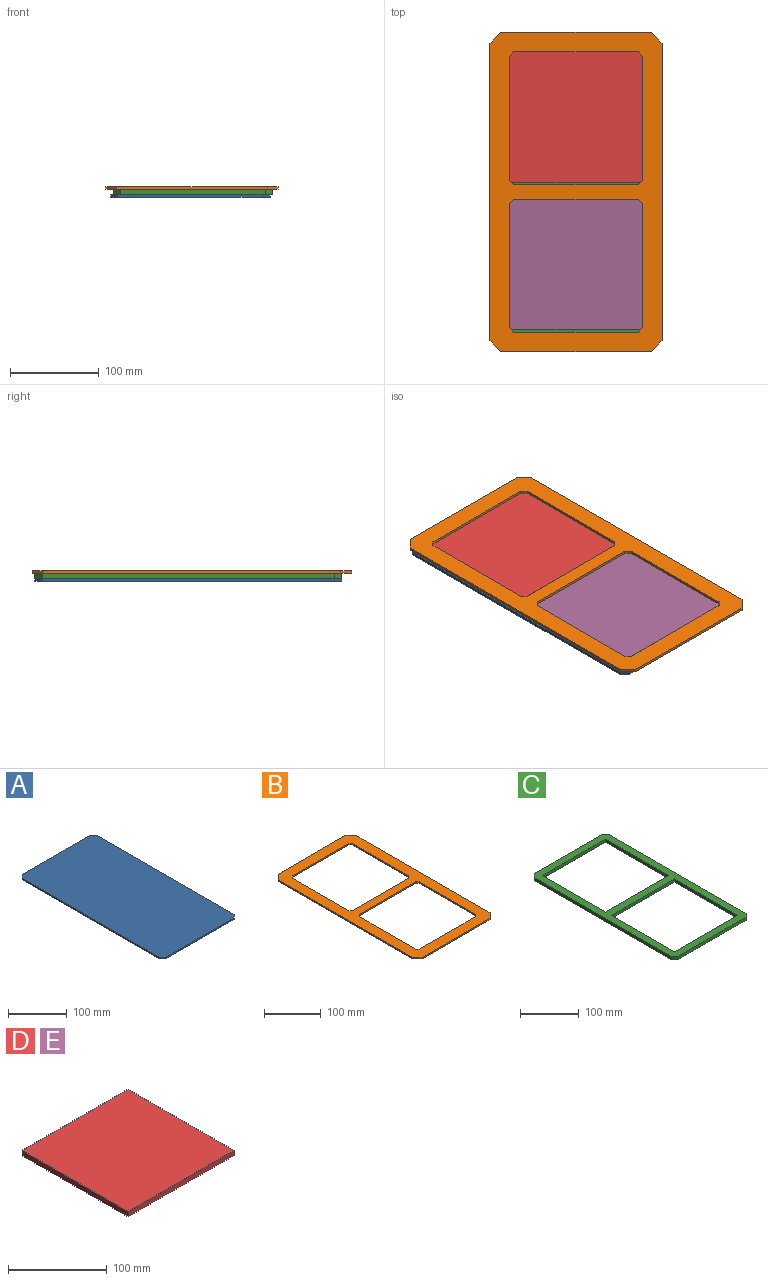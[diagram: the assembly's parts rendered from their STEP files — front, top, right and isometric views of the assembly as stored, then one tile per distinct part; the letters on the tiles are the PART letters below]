
ASSEMBLY  parts=5 mates=4
PART A: 10 faces, bbox 180x346x3 mm
  f0: plane 8.2x8.2mm, normal (-0.71,0.71,0), area 34.8mm2, adj f1,f7,f8,f9
  f1: plane 163.6x3mm, normal (0,1,0), area 490.8mm2, adj f0,f2,f8,f9
  f2: plane 8.2x8.2mm, normal (0.71,0.71,0), area 34.8mm2, adj f1,f3,f8,f9
  f3: plane 329.6x3mm, normal (1,0,0), area 988.8mm2, adj f2,f4,f8,f9
  f4: plane 8.2x8.2mm, normal (0.71,-0.71,0), area 34.8mm2, adj f3,f5,f8,f9
  f5: plane 163.6x3mm, normal (0,-1,0), area 490.8mm2, adj f4,f6,f8,f9
  f6: plane 8.2x8.2mm, normal (-0.71,-0.71,0), area 34.8mm2, adj f5,f7,f8,f9
  f7: plane 329.6x3mm, normal (-1,0,0), area 988.8mm2, adj f0,f6,f8,f9
  f8: plane 346x180mm, normal (0,0,-1), area 62145.5mm2, adj f0,f1,f2,f3,f4,f5,f6,f7
  f9: plane 346x180mm, normal (0,0,1), area 62145.5mm2, adj f0,f1,f2,f3,f4,f5,f6,f7
PART B: 26 faces, bbox 194x360x3 mm
  f0: plane 4.95x4.95mm, normal (0.71,0.71,0), area 21mm2, adj f1,f23,f24,f25
  f1: plane 140.1x3mm, normal (1,0,0), area 420.3mm2, adj f0,f2,f24,f25
  f2: plane 4.95x4.95mm, normal (0.71,-0.71,0), area 21mm2, adj f1,f3,f24,f25
  f3: plane 140.1x3mm, normal (0,-1,0), area 420.3mm2, adj f2,f4,f24,f25
  f4: plane 4.95x4.95mm, normal (-0.71,-0.71,0), area 21mm2, adj f3,f5,f24,f25
  f5: plane 140.1x3mm, normal (-1,0,0), area 420.3mm2, adj f4,f6,f24,f25
  f6: plane 4.95x4.95mm, normal (-0.71,0.71,0), area 21mm2, adj f5,f23,f24,f25
  f7: plane 140.1x3mm, normal (1,0,0), area 420.3mm2, adj f8,f21,f24,f25
  f8: plane 4.95x4.95mm, normal (0.71,-0.71,0), area 21mm2, adj f7,f9,f24,f25
  f9: plane 140.1x3mm, normal (0,-1,0), area 420.3mm2, adj f8,f10,f24,f25
  f10: plane 4.95x4.95mm, normal (-0.71,-0.71,0), area 21mm2, adj f9,f11,f24,f25
  f11: plane 140.1x3mm, normal (-1,0,0), area 420.3mm2, adj f10,f12,f24,f25
  f12: plane 4.95x4.95mm, normal (-0.71,0.71,0), area 21mm2, adj f11,f13,f24,f25
  f13: plane 140.1x3mm, normal (0,1,0), area 420.3mm2, adj f12,f21,f24,f25
  f14: plane 335.4x3mm, normal (-1,0,0), area 1006.2mm2, adj f15,f22,f24,f25
  f15: plane 12.3x12.3mm, normal (-0.71,-0.71,0), area 52.2mm2, adj f14,f16,f24,f25
  f16: plane 169.4x3mm, normal (0,-1,0), area 508.2mm2, adj f15,f17,f24,f25
  f17: plane 12.3x12.3mm, normal (0.71,-0.71,0), area 52.2mm2, adj f16,f18,f24,f25
  f18: plane 335.4x3mm, normal (1,0,0), area 1006.2mm2, adj f17,f19,f24,f25
  f19: plane 12.3x12.3mm, normal (0.71,0.71,0), area 52.2mm2, adj f18,f20,f24,f25
  f20: plane 169.4x3mm, normal (0,1,0), area 508.2mm2, adj f19,f22,f24,f25
  f21: plane 4.95x4.95mm, normal (0.71,0.71,0), area 21mm2, adj f7,f13,f24,f25
  f22: plane 12.3x12.3mm, normal (-0.71,0.71,0), area 52.2mm2, adj f14,f20,f24,f25
  f23: plane 140.1x3mm, normal (0,1,0), area 420.3mm2, adj f0,f6,f24,f25
  f24: plane 360x194mm, normal (0,0,1), area 24635.3mm2, adj f0,f1,f2,f3,f4,f5,f6,f7
  f25: plane 360x194mm, normal (0,0,-1), area 24635.3mm2, adj f0,f1,f2,f3,f4,f5,f6,f7
PART C: 18 faces, bbox 180x346x6.4 mm
  f0: plane 163.6x6.4mm, normal (0,1,0), area 1047mm2, adj f1,f15,f16,f17
  f1: plane 8.2x8.2mm, normal (-0.71,0.71,0), area 74.2mm2, adj f0,f2,f16,f17
  f2: plane 329.6x6.4mm, normal (-1,0,0), area 2109.4mm2, adj f1,f3,f16,f17
  f3: plane 8.2x8.2mm, normal (-0.71,-0.71,0), area 74.2mm2, adj f2,f4,f16,f17
  f4: plane 163.6x6.4mm, normal (0,-1,0), area 1047mm2, adj f3,f5,f16,f17
  f5: plane 8.2x8.2mm, normal (0.71,-0.71,0), area 74.2mm2, adj f4,f6,f16,f17
  f6: plane 329.6x6.4mm, normal (1,0,0), area 2109.4mm2, adj f5,f15,f16,f17
  f7: plane 152x6.4mm, normal (0,-1,0), area 972.8mm2, adj f8,f13,f16,f17
  f8: plane 152x6.4mm, normal (-1,0,0), area 972.8mm2, adj f7,f9,f16,f17
  f9: plane 152x6.4mm, normal (0,1,0), area 972.8mm2, adj f8,f13,f16,f17
  f10: plane 152x6.4mm, normal (0,-1,0), area 972.8mm2, adj f11,f14,f16,f17
  f11: plane 152x6.4mm, normal (-1,0,0), area 972.8mm2, adj f10,f12,f16,f17
  f12: plane 152x6.4mm, normal (0,1,0), area 972.8mm2, adj f11,f14,f16,f17
  f13: plane 152x6.4mm, normal (1,0,0), area 972.8mm2, adj f7,f9,f16,f17
  f14: plane 152x6.4mm, normal (1,0,0), area 972.8mm2, adj f10,f12,f16,f17
  f15: plane 8.2x8.2mm, normal (0.71,0.71,0), area 74.2mm2, adj f0,f6,f16,f17
  f16: plane 346x180mm, normal (0,0,1), area 15937.5mm2, adj f0,f1,f2,f3,f4,f5,f6,f7
  f17: plane 346x180mm, normal (0,0,-1), area 15937.5mm2, adj f0,f1,f2,f3,f4,f5,f6,f7
PART D: 6 faces, bbox 152x152x6.4 mm
  f0: plane 152x6.4mm, normal (0,1,0), area 972.8mm2, adj f1,f3,f4,f5
  f1: plane 152x6.4mm, normal (-1,0,0), area 972.8mm2, adj f0,f2,f4,f5
  f2: plane 152x6.4mm, normal (0,-1,0), area 972.8mm2, adj f1,f3,f4,f5
  f3: plane 152x6.4mm, normal (1,0,0), area 972.8mm2, adj f0,f2,f4,f5
  f4: plane 152x152mm, normal (0,0,1), area 23104mm2, adj f0,f1,f2,f3
  f5: plane 152x152mm, normal (0,0,-1), area 23104mm2, adj f0,f1,f2,f3
PART E: same geometry as D
PLACE A t=(-66.16,-0.04,-78.3)mm
PLACE B t=(-64.43,-4.14,-78.3)mm
PLACE C t=(-63.16,-0.04,-78.3)mm
PLACE D t=(-92.17,168.6,-78.3)mm
PLACE E t=(-92.17,2.6,-78.3)mm
MATE planar C.f16 <-> E.f4  axis (0,0,1) through (-14.9,13.7,-71.9)mm
MATE parallel D.f2 <-> E.f0  axis (0,-1,0) through (-16.17,16.6,-75.1)mm
MATE planar C.f17 <-> A.f9  axis (0,0,-1) through (-14.9,13.7,-78.3)mm
MATE planar B.f25 <-> C.f16  axis (0,0,-1) through (-16.17,9.6,-71.9)mm
